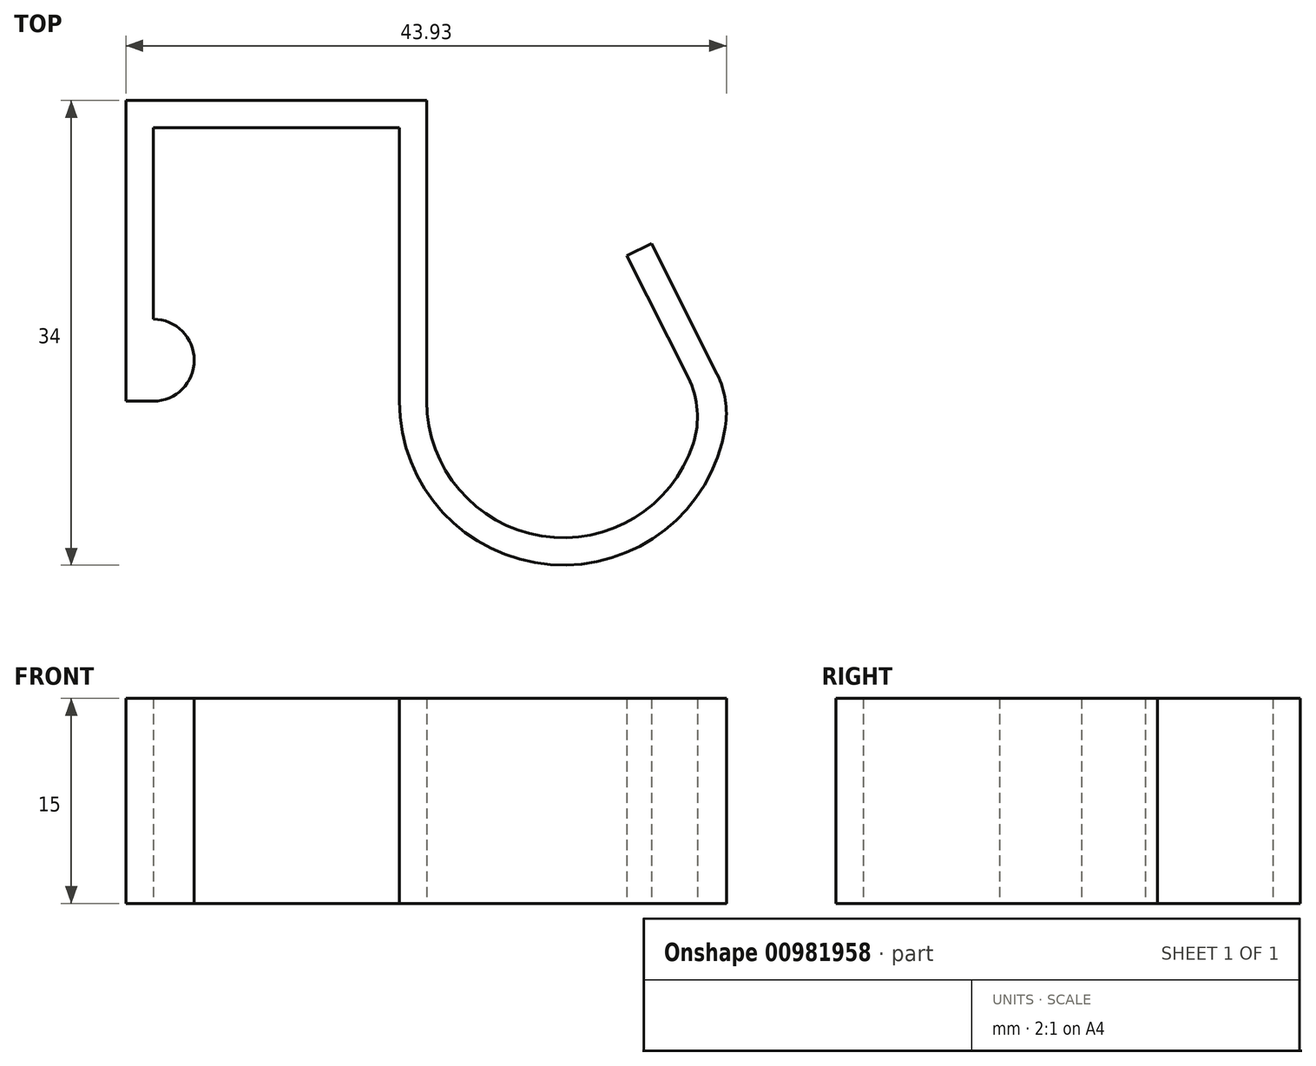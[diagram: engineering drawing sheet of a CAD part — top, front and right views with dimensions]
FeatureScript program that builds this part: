
annotation { "Feature Type Name" : "Feature", "Feature Type Description" : "" }
export const myFeature = defineFeature(function(context is Context, id is Id, definition is map)
    precondition{}
    {
        {
            var Q0;
            Q0=qCreatedBy(makeId("Top.planeOp"),FACE);
            var sketch = newSketch(context, id + "F0", { "sketchPlane" : qUnion([Q0])});
            skLineSegment(sketch, "E0", {"start": v(0, 0) * mm, "end": v(0, 22) * mm});
            skLineSegment(sketch, "E1", {"start": v(0, 22) * mm, "end": v(22, 22) * mm});
            skLineSegment(sketch, "E2", {"start": v(22, 22) * mm, "end": v(22, 0) * mm});
            skArc(sketch, "E3", {"start": v(22, 0) * mm, "mid": v(30.42, -9.87) * mm, "end": v(41.5, -3.12) * mm});
            skArc(sketch, "E4.0", {"start": v(20, 0) * mm, "mid": v(31.05, -11.96) * mm, "end": v(43.85, -1.9) * mm});
            skLineSegment(sketch, "E4.1", {"start": v(20, 20) * mm, "end": v(20, 0) * mm});
            skLineSegment(sketch, "E4.2", {"start": v(2, 20) * mm, "end": v(20, 20) * mm});
            skLineSegment(sketch, "E5", {"start": v(2, 0) * mm, "end": v(0, 0) * mm});
            skArc(sketch, "E6", {"start": v(2, 0) * mm, "mid": v(5, 3) * mm, "end": v(2, 6) * mm});
            skLineSegment(sketch, "E7.trimOffspring", {"start": v(2, 6) * mm, "end": v(2, 20) * mm});
            skLineSegment(sketch, "E8", {"start": v(41.14, 1.7) * mm, "end": v(36.66, 10.65) * mm});
            skLineSegment(sketch, "E9", {"start": v(36.66, 10.65) * mm, "end": v(38.44, 11.54) * mm});
            skLineSegment(sketch, "E10", {"start": v(38.44, 11.54) * mm, "end": v(43.25, 1.96) * mm});
            skPoint(sketch, "E11.visualSharp", {"position": v(42, 0) * mm});
            skArc(sketch, "E11.filletArc", {"start": v(41.5, -3.12) * mm, "mid": v(41.8, -0.67) * mm, "end": v(41.14, 1.7) * mm});
            skPoint(sketch, "E12.visualSharp", {"position": v(43.99, 0.5) * mm});
            skArc(sketch, "E12.filletArc", {"start": v(43.85, -1.9) * mm, "mid": v(43.85, 0.08) * mm, "end": v(43.25, 1.96) * mm});
            skSolve(sketch);
        }
        {
            var Q0;
            Q0=makeQuery(id+"F0.imprint","IMPRINT",FACE,{"disambiguationData":[TD([[makeQuery(id+"F0.imprint","IMPRINT",EDGE,{"derivedFrom":sQuery(id+"F0.wireOp",EDGE,"E0")}),-1.0]])]});
            extrude(context, id + "F1", {"entities" : qUnion([Q0]), "depth" : 15 * mm, "offsetDistance" : 25 * mm});
        }
    });
